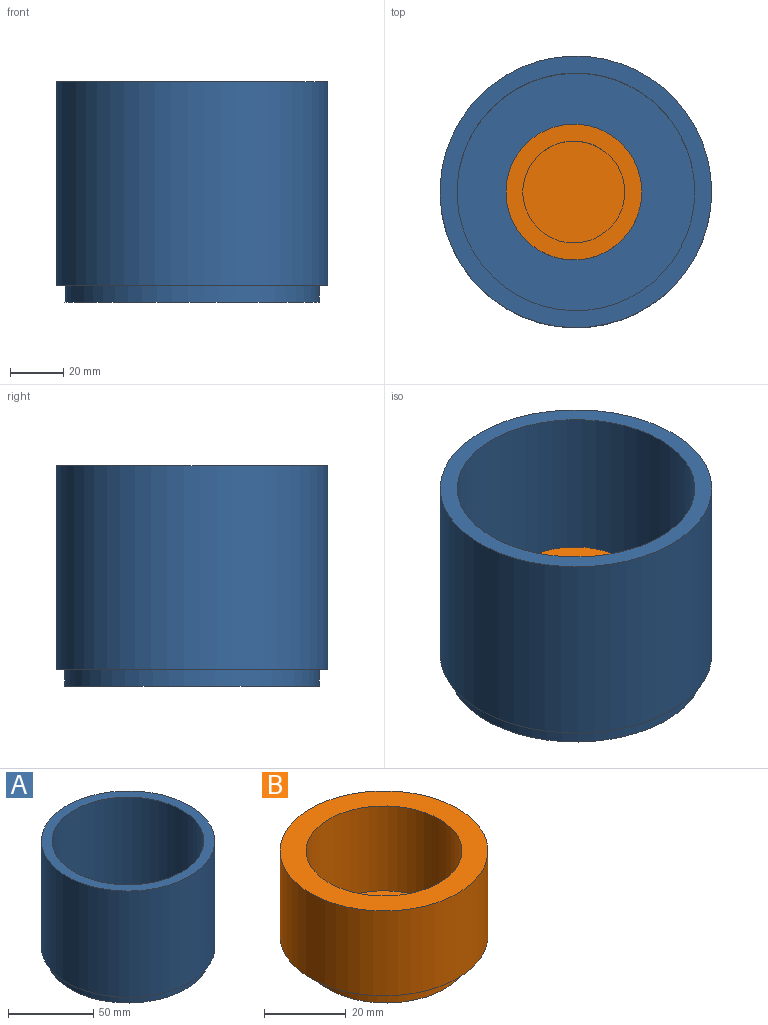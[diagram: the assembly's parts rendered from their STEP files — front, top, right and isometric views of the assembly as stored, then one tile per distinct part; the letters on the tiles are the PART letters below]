
ASSEMBLY  parts=2 mates=1
PART A: 7 faces, bbox 101.6x101.6x82.6 mm
  f0: cylinder r=44.45mm len=88.9mm, axis (0,0,-1), area 21281.7mm2, adj f2,f6
  f1: cylinder r=50.8mm len=101.6mm, axis (0,0,-1), area 24322mm2, adj f2,f3
  f2: plane 101.6x101.6mm, normal (0,0,1), area 1900.2mm2, adj f0,f1
  f3: plane 101.6x101.6mm, normal (0,0,-1), area 993.6mm2, adj f1,f5
  f4: plane 95.17x95.17mm, normal (0,0,-1), area 7113.8mm2, adj f5
  f5: cylinder r=47.59mm len=95.17mm, axis (0,0,1), area 1898.6mm2, adj f3,f4
  f6: plane 88.9x88.9mm, normal (0,0,1), area 6207.2mm2, adj f0
PART B: 7 faces, bbox 50.8x50.8x31.8 mm
  f0: cylinder r=19.05mm len=38.1mm, axis (0,0,-1), area 3040.2mm2, adj f2,f6
  f1: cylinder r=25.4mm len=50.8mm, axis (0,0,-1), area 4053.7mm2, adj f2,f3
  f2: plane 50.8x50.8mm, normal (0,0,1), area 886.7mm2, adj f0,f1
  f3: plane 50.8x50.8mm, normal (0,0,-1), area 774.3mm2, adj f1,f5
  f4: plane 39.93x39.93mm, normal (0,0,-1), area 1252.5mm2, adj f5
  f5: cylinder r=19.97mm len=39.93mm, axis (0,0,1), area 796.7mm2, adj f3,f4
  f6: plane 38.1x38.1mm, normal (0,0,1), area 1140.1mm2, adj f0
PLACE A at identity
PLACE B t=(-115.04,0,6.35)mm
MATE slider B.f5 <-> A.f0  axis (0,0,-1) through (-73.26,0,0)mm
